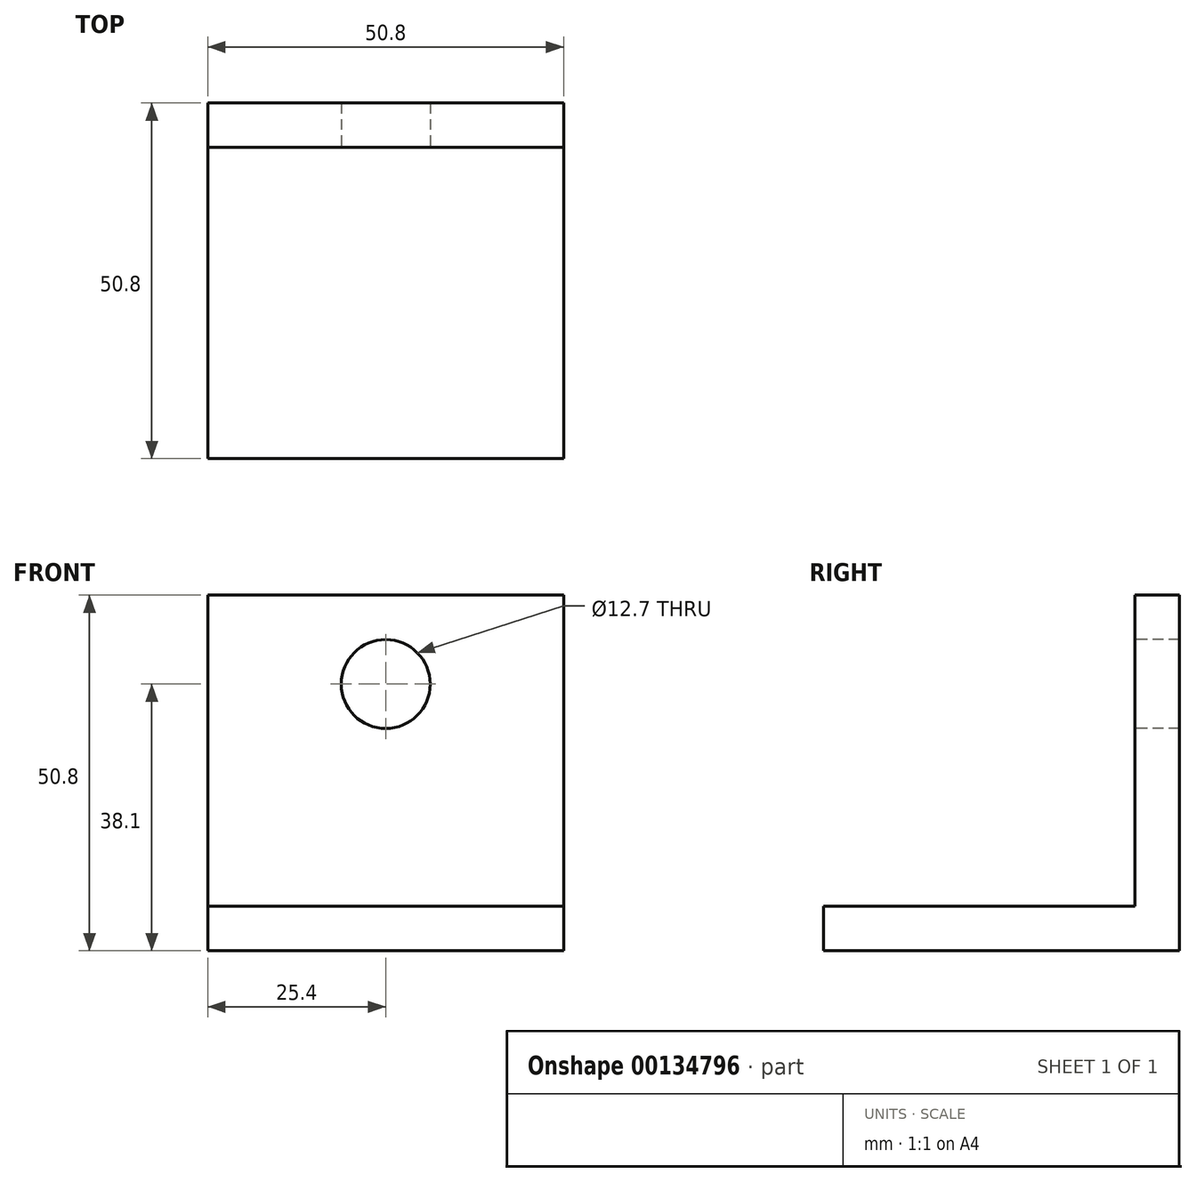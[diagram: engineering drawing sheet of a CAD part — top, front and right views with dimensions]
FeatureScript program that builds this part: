
annotation { "Feature Type Name" : "Feature", "Feature Type Description" : "" }
export const myFeature = defineFeature(function(context is Context, id is Id, definition is map)
    precondition{}
    {
        {
            var Q0;
            Q0=qCreatedBy(makeId("Right.planeOp"),FACE);
            var sketch = newSketch(context, id + "F0", { "sketchPlane" : qUnion([Q0])});
            skLineSegment(sketch, "E0", {"start": v(-50.8, 0) * mm, "end": v(0, 0) * mm});
            skLineSegment(sketch, "E1", {"start": v(0, 0) * mm, "end": v(0, 50.8) * mm});
            skLineSegment(sketch, "E2", {"start": v(0, 50.8) * mm, "end": v(-6.35, 50.8) * mm});
            skLineSegment(sketch, "E3", {"start": v(-6.35, 50.8) * mm, "end": v(-6.35, 6.35) * mm});
            skLineSegment(sketch, "E4", {"start": v(-6.35, 6.35) * mm, "end": v(-50.8, 6.35) * mm});
            skLineSegment(sketch, "E5", {"start": v(-50.8, 6.35) * mm, "end": v(-50.8, 0) * mm});
            skSolve(sketch);
        }
        {
            var Q0;
            Q0=makeQuery(id+"F0.imprint","IMPRINT",FACE,{"disambiguationData":[TD([[makeQuery(id+"F0.imprint","IMPRINT",EDGE,{"derivedFrom":sQuery(id+"F0.wireOp",EDGE,"E0")}),1.0]])]});
            extrude(context, id + "F1", {"entities" : qUnion([Q0]), "depth" : 50.8 * mm, "symmetric" : true});
        }
        {
            var Q0;
            Q0=makeQuery(id+"F1.opExtrude","SWEPT_FACE",FACE,{"disambiguationData":[OSD([sQuery(id+"F0.wireOp",EDGE,"E3")])]});
            var sketch = newSketch(context, id + "F2", { "sketchPlane" : qUnion([Q0])});
            skPoint(sketch, "E6", {"position": v(0, 38.1) * mm});
            skSolve(sketch);
        }
        {
            var Q0;
            Q0=sQuery(id+"F2.wireOp",VERTEX,"E6");
            var Q1;
            Q1=makeQuery(id+"F1.opExtrude","SWEPT_BODY",BODY,{"disambiguationData":[OSD([sQuery(id+"F0.wireOp",EDGE,"E0"),sQuery(id+"F0.wireOp",EDGE,"E1"),sQuery(id+"F0.wireOp",EDGE,"E2"),sQuery(id+"F0.wireOp",EDGE,"E3"),sQuery(id+"F0.wireOp",EDGE,"E4"),sQuery(id+"F0.wireOp",EDGE,"E5")])]});
            hole(context, id + "F3", {"style" : HoleStyle.SIMPLE, "endStyle" : HoleEndStyle.THROUGH, "holeDiameter" : 12.7 * mm, "locations" : qUnion([Q0]), "scope" : qUnion([Q1]), "isTappedThrough" : true});
        }
    });
